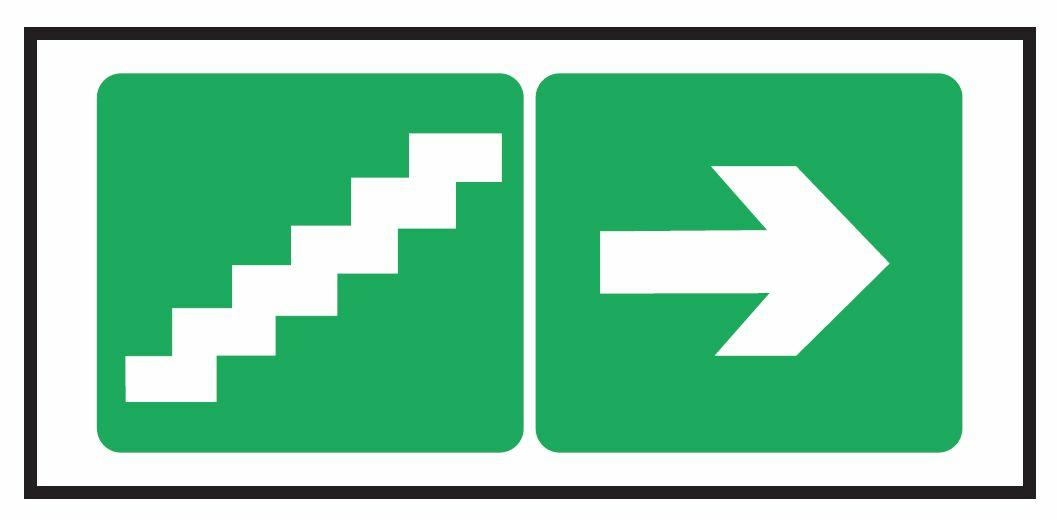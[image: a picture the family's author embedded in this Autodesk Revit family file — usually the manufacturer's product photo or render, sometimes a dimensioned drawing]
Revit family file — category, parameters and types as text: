
# Revit family: Legrand_Emergencia_URA_ONE_EXPORT_EN
name_source: partatom
category: Luminaires
units: mm (PartAtom-declared; Revit-internal decimal feet)

## family parameters
Cote de connecteur circulaire = Utiliser le diamètre
Couper avec des vides une fois chargée = Non
Hôte = Face
Partagée = Non
Point de calcul de pièce = Non
Source d'éclairage = Oui
Type d'élément = Normal

## types (16) — shared parameters
Angle de l'inclinaison = 90.00°
BAES_FULL_WARRANTY_PERIOD = 2
CATEGORY = Self-contained
COLOUR_HOUSING = White
DEGREE_OF_PROTECTION_(IP) = IP42
Elévation par défaut = 1219 mm
FUNCTION = EL unit
Filtre de couleur = 16777215
General Conditions of Use = https://export.legrand.com
Gradation des changements de température de couleur de lampe = <Aucun>
HEIGHT/DEPTH = 41
LABELLING_TYPE = Sticker
LAMP_TYPE = Fluorescent lamp
LENGTH = 210
MATERIAL_COVER = Plastic. opal
MATERIAL_HOUSING = Plastic
MOUNTING_METHOD = Built-in
NOMINAL_VOLTAGE_(MAX) = 230
NOMINAL_VOLTAGE_(MIN) = 230
POWER_SUPPLY_SYSTEM = Peripheral (individual battery)
PRODUCT_FORMAT = Rectangle
PROTECTION_CLASS = II
VOLTAGE_TYPE = AC
WIDTH = 110

## per-type parameters (varying)
| type | ARTICLE_NUMBER | AUTONOMY | BATTERY_QUALITY | Fichier de distribution photométrique | LAMP_POWER | LUMINOUS_FLUX_AT_EMERGENCY_OPERATION | MONITORING_EQUIPEMENT | REF_SPARE_BATTERY | WIRING_SYSTEM |
| URAONE NM 70LM 1H IP42 STD | 661620 | 1 | NiCd | 661620.ies | 7 | 70 | None | 660972 | Standby switching |
| URAONE NM 100LM 1H IP42 STD | 661621 | 1 | NiCd | 661621.ies | 10 | 100 | None | 660972 | Standby switching |
| URAONE NM 160LM 1H IP42 STD | 661622 | 1 | NiCd | 661622.ies | 16 | 160 | None | 660972 | Standby switching |
| URA ONE NM 200LM 1H IP42 STD | 661623 | 1 | NiCd | 661623.ies | 20 | 200 | None | 660972 | Standby switching |
| URA ONE NM 350LM 1H IP42 STD | 661624 | 1 | NiCd | 661624.ies | 35 | 350 | None | 660962 | Standby switching |
| URAONE M-NM 100LM 1H IP42 STD | 661631 | 1 | NiCd | 661631.ies | 10 | 100 | None | 660972 | Continuous circuit/emergency cicuit |
| URAONE M-NM 160LM 1H IP42 STD | 661632 | 1 | NiCd | 661632.ies | 16 | 160 | None | 660972 | Continuous circuit/emergency cicuit |
| URAONE M-NM 200LM 1H IP42 STD | 661633 | 1 | NiCd | 661633.ies | 20 | 200 | None | 660962 | Continuous circuit/emergency cicuit |
| URAONE M-NM 350LM 1H IP42 STD | 661634 | 1 | NiCd | 661634.ies | 35 | 350 | None | 660962 | Continuous circuit/emergency cicuit |
| URAONE M-NM 100LM 3H IP42 STD | 661640 | 3 | NiMh | 661640.ies | 10 | 100 | None | 660971 | Continuous circuit/emergency cicuit |
| URAONE M-NM 200LM 2H IP42 STD | 661642 | 2 | NiMh | 661642.ies | 20 | 200 | None | 660971 | Continuous circuit/emergency cicuit |
| URAONE M-NM 100LM 1H IP42 ADR | 662631 | 1 | NiCd | 662631.ies | 10 | 100 | Automatic self test | 660972 | Continuous circuit/emergency cicuit |
| URAONE M-NM 200LM 1H IP42 ADR | 662633 | 1 | NiCd | 662633.ies | 20 | 200 | Automatic self test | 660962 | Continuous circuit/emergency cicuit |
| URAONE M-NM 350LM 1H IP42 ADR | 662634 | 1 | NiMh | 662634.ies | 35 | 350 | Automatic self test | 660971 | Continuous circuit/emergency cicuit |
| URAONE M-NM 100LM 3H IP42 ADR | 662640 | 3 | NiMh | 662640.ies | 10 | 100 | Automatic self test | 660971 | Continuous circuit/emergency cicuit |
| URAONE M-NM 200LM 2H IP42 ADR | 662642 | 2 | NiMh | 662642.ies | 20 | 200 | Automatic self test | 660971 | Continuous circuit/emergency cicuit |

note: column(s) folded — value = type name in every type: DESCRIPTION
